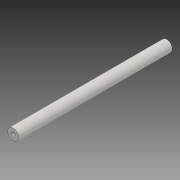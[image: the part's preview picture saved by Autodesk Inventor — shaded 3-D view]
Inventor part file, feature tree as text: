
AUTODESK INVENTOR PART (.ipt)
format: ipt  version: 2017 (Build 210142000, 142)  size: 74,240 bytes
history: native  units: mm
features: extrude x1, sketch x1
ambient origin geometry x8: Origin, YZ Plane, XZ Plane, XY Plane, X Axis, Y Axis, Z Axis, Center Point
bodies: Solid1 (feature_tree)
feature tree (2):
  extrude  "Extrusion1"  Depth=10.0mm
  sketch  "Sketch1"  dims[d0=4.0mm d1=10.0mm d2=140.0mm d3=0.0mm]
